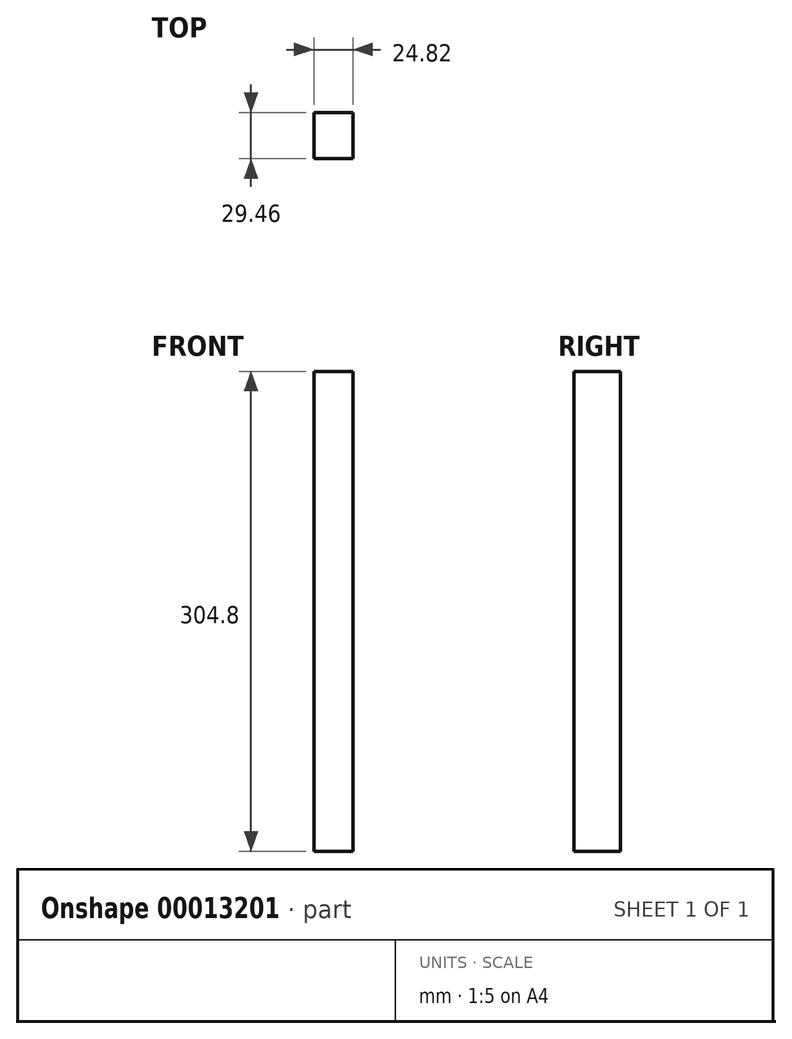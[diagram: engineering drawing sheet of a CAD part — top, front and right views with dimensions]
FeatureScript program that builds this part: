
annotation { "Feature Type Name" : "Feature", "Feature Type Description" : "" }
export const myFeature = defineFeature(function(context is Context, id is Id, definition is map)
    precondition{}
    {
        {
            var Q0;
            Q0=qCreatedBy(makeId("Top.planeOp"),FACE);
            var sketch = newSketch(context, id + "F0", { "sketchPlane" : qUnion([Q0])});
            skLineSegment(sketch, "E0.bottom", {"start": v(12.4, -14.73) * mm, "end": v(-12.4, -14.73) * mm});
            skLineSegment(sketch, "E0.top", {"start": v(12.4, 14.73) * mm, "end": v(-12.4, 14.73) * mm});
            skLineSegment(sketch, "E0.left", {"start": v(12.4, -14.73) * mm, "end": v(12.4, 14.73) * mm});
            skLineSegment(sketch, "E0.right", {"start": v(-12.4, -14.73) * mm, "end": v(-12.4, 14.73) * mm});
            skPoint(sketch, "E0.middle", {"position": v(0, 0) * mm});
            skSolve(sketch);
        }
        {
            var Q0;
            Q0 = qSketchRegion(id + "F0", true);
            extrude(context, id + "F1", {"entities" : qUnion([Q0]), "depth" : 304.8 * mm, "offsetDistance" : 25.4 * mm});
        }
    });
